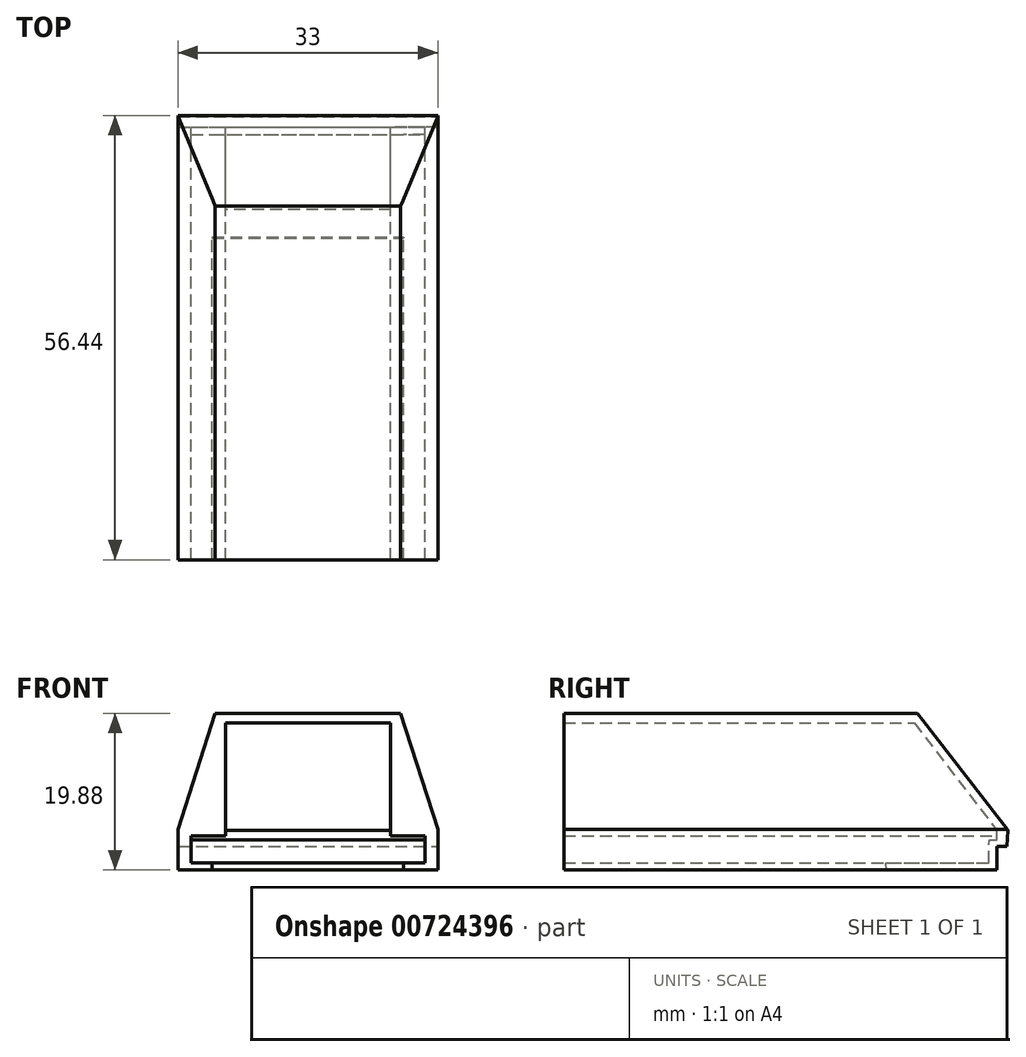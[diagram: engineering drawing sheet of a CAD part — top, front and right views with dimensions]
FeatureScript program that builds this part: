
annotation { "Feature Type Name" : "Feature", "Feature Type Description" : "" }
export const myFeature = defineFeature(function(context is Context, id is Id, definition is map)
    precondition{}
    {
        {
            var Q0;
            Q0=qCreatedBy(makeId("Front.planeOp"),FACE);
            var sketch = newSketch(context, id + "F0", { "sketchPlane" : qUnion([Q0])});
            skLineSegment(sketch, "E0.top", {"start": v(10, -9.72) * mm, "end": v(-10.5, -9.72) * mm});
            skLineSegment(sketch, "E0.left", {"start": v(10, 2.28) * mm, "end": v(10, -9.72) * mm});
            skLineSegment(sketch, "E0.right", {"start": v(-10.5, 2.28) * mm, "end": v(-10.5, -9.72) * mm});
            skPoint(sketch, "E0.middle", {"position": v(-0.25, -3.72) * mm});
            skLineSegment(sketch, "E1", {"start": v(10, 2.28) * mm, "end": v(14, 2.28) * mm});
            skLineSegment(sketch, "E2", {"start": v(14, 2.28) * mm, "end": v(14, 1.03) * mm});
            skLineSegment(sketch, "E3", {"start": v(14, 1.03) * mm, "end": v(11.25, 1.03) * mm});
            skLineSegment(sketch, "E4", {"start": v(11.25, 1.03) * mm, "end": v(11.25, -10.97) * mm});
            skLineSegment(sketch, "E5", {"start": v(11.25, -10.97) * mm, "end": v(-11.75, -10.97) * mm});
            skLineSegment(sketch, "E6", {"start": v(-11.75, -10.97) * mm, "end": v(-11.75, 1.03) * mm});
            skLineSegment(sketch, "E7", {"start": v(-11.75, 1.03) * mm, "end": v(-14.5, 1.03) * mm});
            skLineSegment(sketch, "E8", {"start": v(-14.5, 1.03) * mm, "end": v(-14.5, 2.28) * mm});
            skLineSegment(sketch, "E9", {"start": v(-14.5, 2.28) * mm, "end": v(-10.5, 2.28) * mm});
            skSolve(sketch);
        }
        {
            var Q0;
            Q0=qCreatedBy(makeId("Front.planeOp"),FACE);
            var sketch = newSketch(context, id + "F1", { "sketchPlane" : qUnion([Q0])});
            skLineSegment(sketch, "E10", {"start": v(-12.15, 0) * mm, "end": v(-12.15, 0.9) * mm});
            skLineSegment(sketch, "E11", {"start": v(-12.15, 0.9) * mm, "end": v(-14.85, 0.9) * mm});
            skLineSegment(sketch, "E12", {"start": v(-14.85, 0.9) * mm, "end": v(-14.85, 4.3) * mm});
            skLineSegment(sketch, "E13", {"start": v(0, 19.88) * mm, "end": v(-11.78, 19.88) * mm});
            skLineSegment(sketch, "E14", {"start": v(-16.5, 0) * mm, "end": v(-12.15, 0) * mm});
            skLineSegment(sketch, "E15", {"start": v(-14.85, 4.3) * mm, "end": v(-10.5, 4.3) * mm});
            skLineSegment(sketch, "E16", {"start": v(-10.5, 4.3) * mm, "end": v(-10.5, 18.68) * mm});
            skLineSegment(sketch, "E17", {"start": v(-16.5, 5.12) * mm, "end": v(-16.5, 0) * mm});
            skLineSegment(sketch, "E18", {"start": v(0, 19.88) * mm, "end": v(0, 18.68) * mm});
            skLineSegment(sketch, "E19", {"start": v(-10.5, 18.68) * mm, "end": v(0, 18.68) * mm});
            skLineSegment(sketch, "E20", {"start": v(-16.5, 5.12) * mm, "end": v(-11.78, 19.88) * mm});
            skSolve(sketch);
        }
        {
            var Q0;
            Q0=qCreatedBy(makeId("Right.planeOp"),FACE);
            var sketch = newSketch(context, id + "F2", { "sketchPlane" : qUnion([Q0])});
            skLineSegment(sketch, "E21", {"start": v(18.12, 18.98) * mm, "end": v(28.94, 5.03) * mm});
            skLineSegment(sketch, "E22", {"start": v(28.94, 5.03) * mm, "end": v(28.8, 3) * mm});
            skLineSegment(sketch, "E23", {"start": v(27.5, 0) * mm, "end": v(13.5, 0) * mm});
            skLineSegment(sketch, "E24", {"start": v(13.4, 0.9) * mm, "end": v(26.5, 0.9) * mm});
            skLineSegment(sketch, "E25", {"start": v(13.4, 0.9) * mm, "end": v(13.5, 0) * mm});
            skLineSegment(sketch, "E26", {"start": v(27.5, 0) * mm, "end": v(27.5, 3) * mm});
            skLineSegment(sketch, "E27", {"start": v(28.8, 3) * mm, "end": v(27.5, 3) * mm});
            skLineSegment(sketch, "E28", {"start": v(26.53, 3.79) * mm, "end": v(26.5, 0.9) * mm});
            skLineSegment(sketch, "E29", {"start": v(27.5, 5.12) * mm, "end": v(27.5, 3.79) * mm});
            skLineSegment(sketch, "E30", {"start": v(27.5, 5.03) * mm, "end": v(16.8, 18.95) * mm});
            skLineSegment(sketch, "E31", {"start": v(27.5, 3.79) * mm, "end": v(26.53, 3.79) * mm});
            skLineSegment(sketch, "E32", {"start": v(18.12, 18.98) * mm, "end": v(16.8, 18.95) * mm});
            skSolve(sketch);
        }
        {
            var Q0;
            Q0 = qSketchRegion(id + "F1", true);
            extrude(context, id + "F3", {"entities" : qUnion([Q0]), "endBound" : BoundingType.SYMMETRIC, "depth" : 55 * mm, "offsetDistance" : 25 * mm});
        }
        {
            var Q0;
            Q0 = qSketchRegion(id + "F2", true);
            extrude(context, id + "F4", {"entities" : qUnion([Q0]), "operationType" : NewBodyOperationType.ADD, "oppositeDirection" : true, "depth" : 16.5 * mm, "offsetDistance" : 25 * mm});
        }
        {
            var Q0;
            Q0=qCreatedBy(makeId("Front.planeOp"),FACE);
            var sketch = newSketch(context, id + "F5", { "sketchPlane" : qUnion([Q0])});
            skLineSegment(sketch, "E33", {"start": v(-16.5, 5.12) * mm, "end": v(-16.5, 0) * mm});
            skLineSegment(sketch, "E34", {"start": v(-16.5, 5.12) * mm, "end": v(-11.78, 19.88) * mm});
            skLineSegment(sketch, "E35", {"start": v(-11.78, 19.88) * mm, "end": v(-17.82, 19.88) * mm});
            skLineSegment(sketch, "E36", {"start": v(-17.82, 19.88) * mm, "end": v(-17.82, 0) * mm});
            skLineSegment(sketch, "E37", {"start": v(-17.82, 0) * mm, "end": v(-16.5, 0) * mm});
            skSolve(sketch);
        }
        {
            var Q0;
            Q0 = qSketchRegion(id + "F5", true);
            extrude(context, id + "F6", {"entities" : qUnion([Q0]), "operationType" : NewBodyOperationType.REMOVE, "endBound" : BoundingType.SYMMETRIC, "oppositeDirection" : true, "depth" : 60 * mm, "offsetDistance" : 25 * mm});
        }
        {
            var Q0;
            Q0=makeQuery(id+"F3.opExtrude","SWEPT_BODY",BODY,{"disambiguationData":[OSD([sQuery(id+"F1.wireOp",EDGE,"E10"),sQuery(id+"F1.wireOp",EDGE,"E11"),sQuery(id+"F1.wireOp",EDGE,"E12"),sQuery(id+"F1.wireOp",EDGE,"E13"),sQuery(id+"F1.wireOp",EDGE,"E14"),sQuery(id+"F1.wireOp",EDGE,"E15"),sQuery(id+"F1.wireOp",EDGE,"E16"),sQuery(id+"F1.wireOp",EDGE,"E17"),sQuery(id+"F1.wireOp",EDGE,"E18"),sQuery(id+"F1.wireOp",EDGE,"E19"),sQuery(id+"F1.wireOp",EDGE,"E20")])]});
            var Q1;
            Q1=qCreatedBy(makeId("Right.planeOp"),FACE);
            mirror(context, id + "F7", {"operationType" : NewBodyOperationType.ADD, "entities" : qUnion([Q0]), "mirrorPlane" : qUnion([Q1])});
        }
        {
            var Q0;
            Q0=qCreatedBy(makeId("Right.planeOp"),FACE);
            var sketch = newSketch(context, id + "F8", { "sketchPlane" : qUnion([Q0])});
            skLineSegment(sketch, "E38", {"start": v(17.4, 19.9) * mm, "end": v(28.94, 5.03) * mm});
            skLineSegment(sketch, "E39", {"start": v(28.94, 5.03) * mm, "end": v(28.8, 3) * mm});
            skLineSegment(sketch, "E40", {"start": v(27.5, 0) * mm, "end": v(27.5, 3) * mm});
            skLineSegment(sketch, "E41", {"start": v(28.8, 3) * mm, "end": v(27.5, 3) * mm});
            skLineSegment(sketch, "E42", {"start": v(31.29, 20.14) * mm, "end": v(31.46, 0) * mm});
            skLineSegment(sketch, "E43", {"start": v(31.46, 0) * mm, "end": v(27.5, 0) * mm});
            skLineSegment(sketch, "E44", {"start": v(31.29, 20.14) * mm, "end": v(17.4, 19.9) * mm});
            skSolve(sketch);
        }
        {
            var Q0;
            Q0 = qSketchRegion(id + "F8", true);
            extrude(context, id + "F9", {"entities" : qUnion([Q0]), "operationType" : NewBodyOperationType.REMOVE, "endBound" : BoundingType.SYMMETRIC, "depth" : 35 * mm, "offsetDistance" : 25 * mm});
        }
    });
